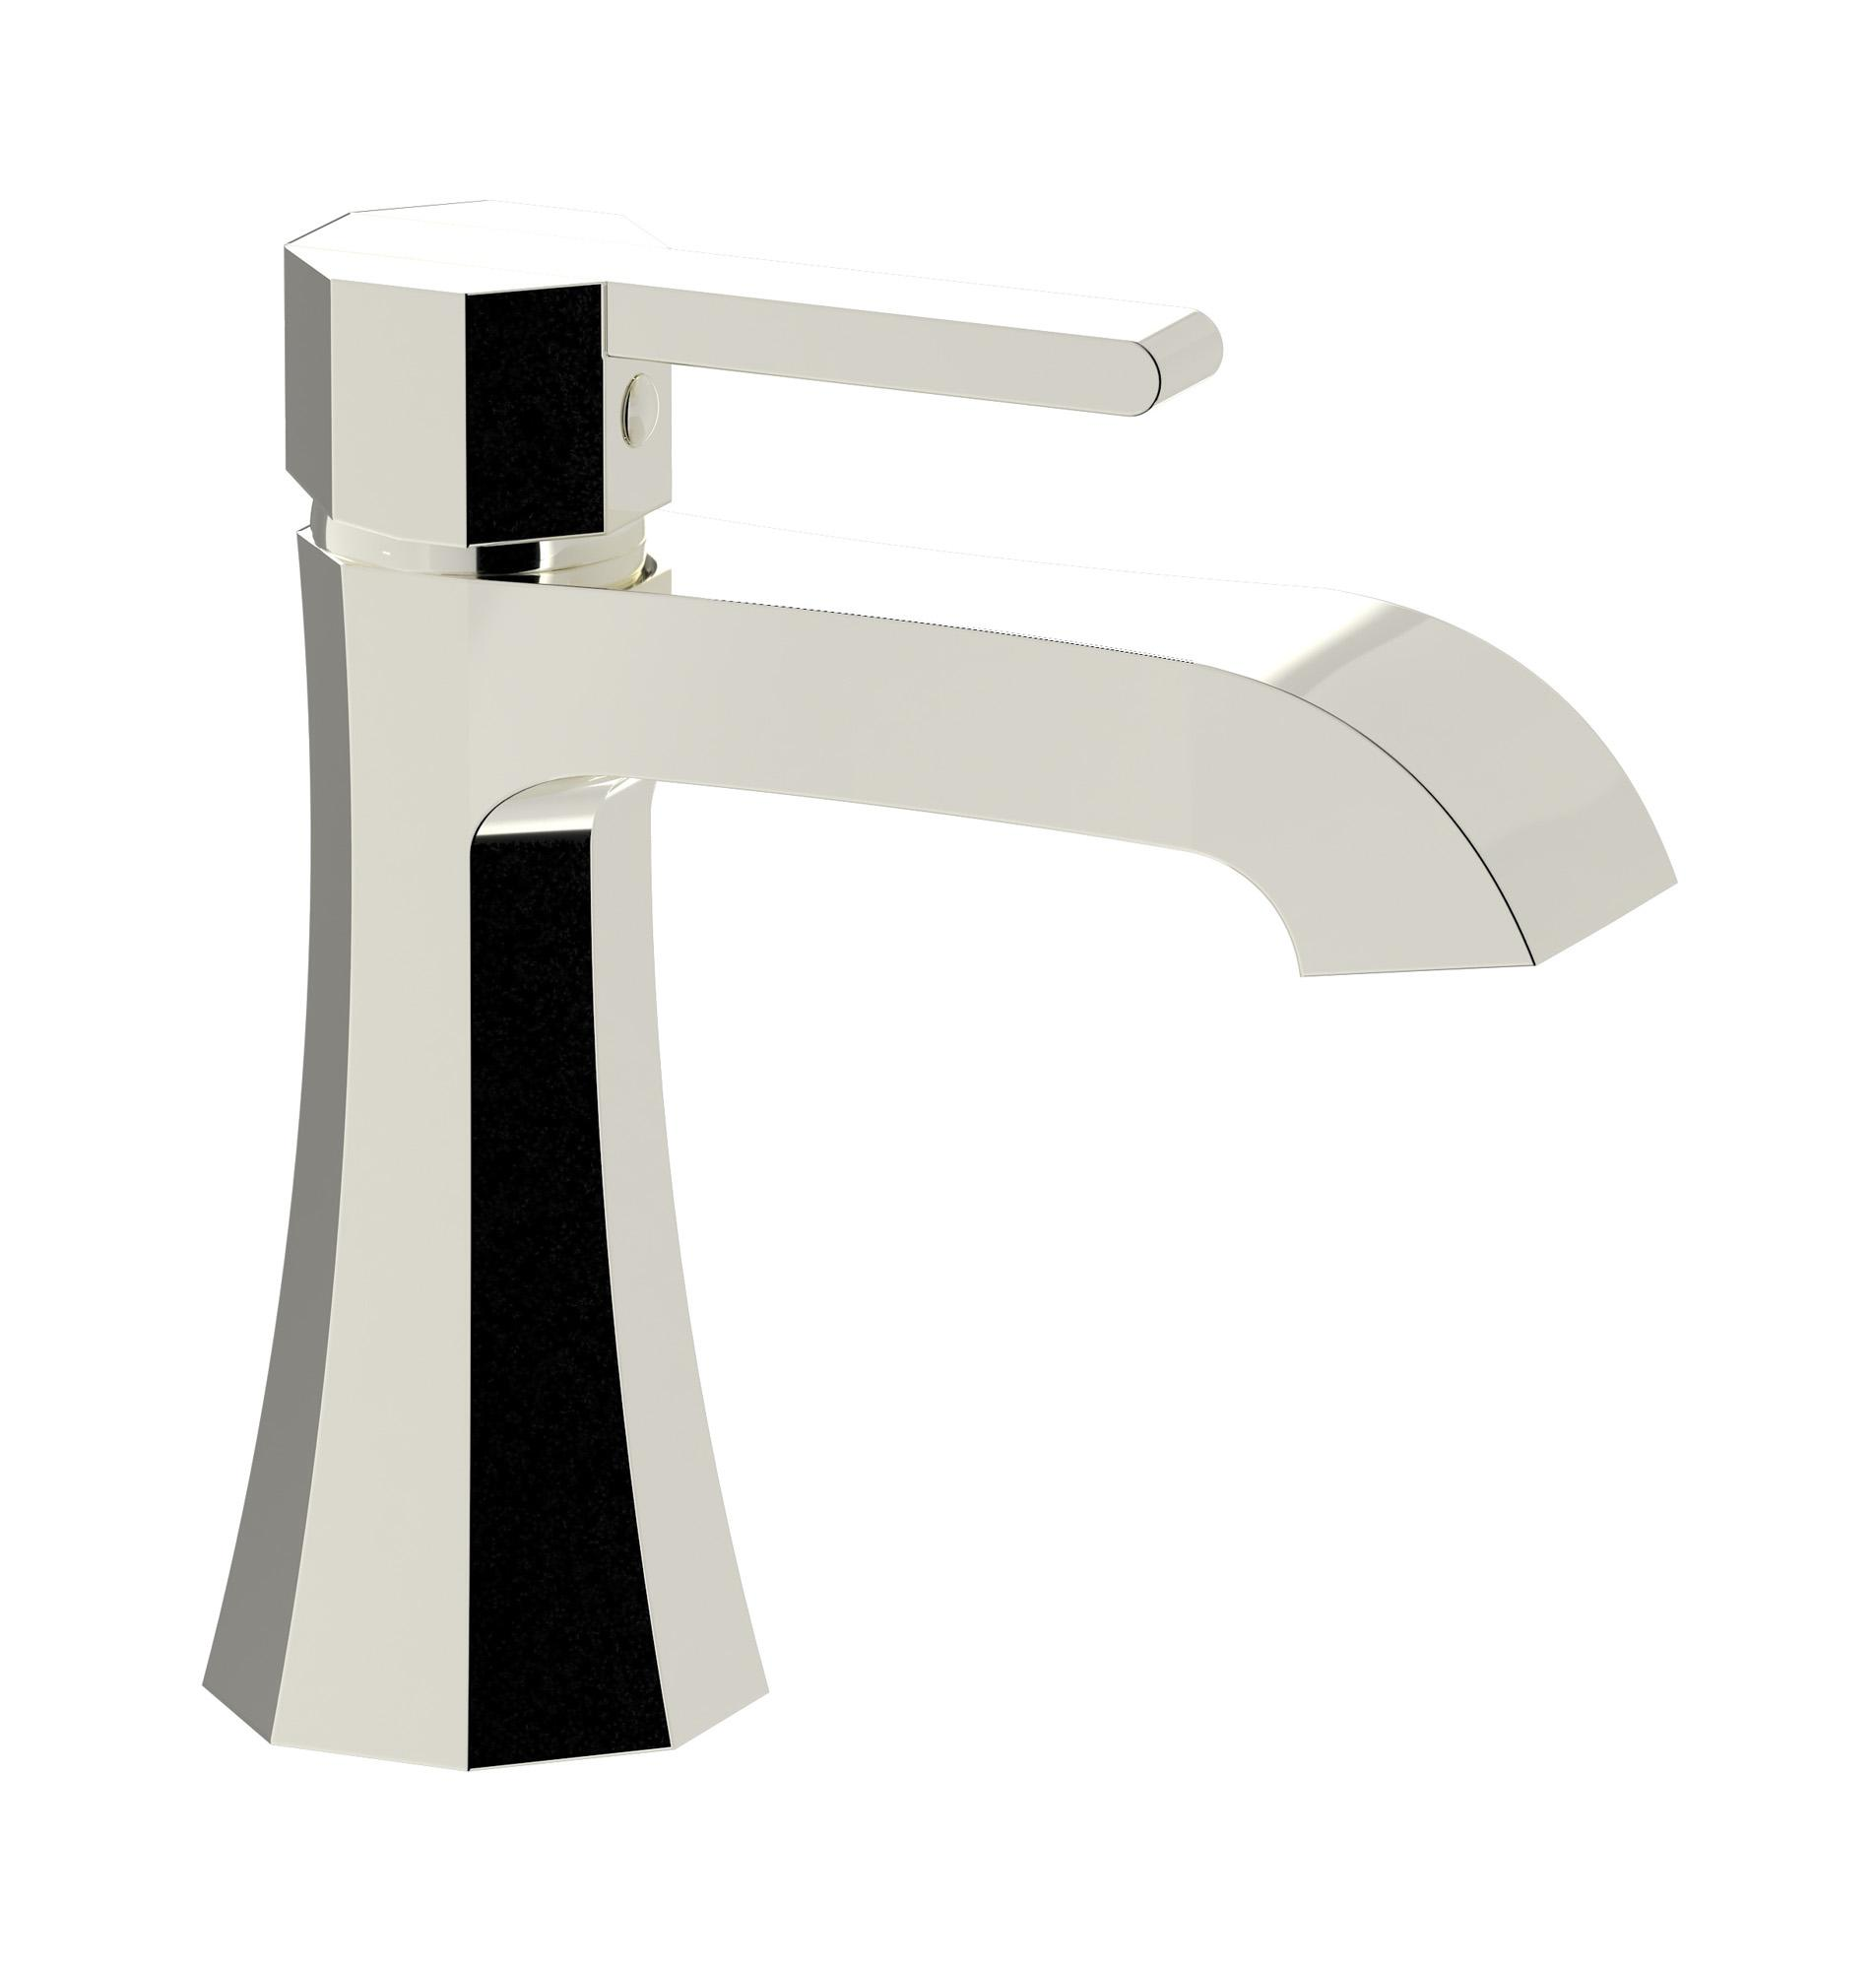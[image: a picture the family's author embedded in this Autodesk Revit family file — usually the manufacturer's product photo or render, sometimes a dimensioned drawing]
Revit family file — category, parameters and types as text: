
# Revit family: BL200
name_source: partatom
category: Apparecchi idraulici
units: mm (PartAtom-declared; Revit-internal decimal feet)

## family parameters
Basato su piano di lavoro = No
Condiviso = No
Mantieni orientamento annotazione = No
Numero OmniClass = 23.45.55.17
Punto di calcolo locali = No
Quota connettore circolare = Usa diametro
Sempre verticale = Sì
Taglio con vuoti quando caricato = No
Tipo di parte = Normale
Titolo OmniClass = Mixing Faucets

## types (7) — shared parameters
Cold water inlet = 10 mm  [stored 0.0328084 ft]
Commenti sul tipo = Washbasin
Connessione CW = No
Connessione HW = No
Connessione di scarico = No
Connessione di ventilazione = No
Descrizione = Monohole washbasin mixer complete with drain
Hot water inlet = 10 mm  [stored 0.0328084 ft]
Produttore = IB Rubinetterie S.p.A.
URL = https://www.weareib.it
zero-valued in all types: Prospetto di default

## per-type parameters (varying)
| type | Finishes surface | Immagine tipo | Modello |
| Chrome | IB_Chrome | BL200CC.jpg | BL200CC |
| Platinum | IB_Platinum | BL200PL.jpg | BL200PL |
| Pale gold | IB_Pale gold | BL200II.jpg | BL200II |
| Rose gold | IB_Rose gold | BL200RS.jpg | BL200RS |
| Gold | IB_gold | BL200OO.jpg | BL200OO |
| Modern Bronze | IB_Modern bronze | BL200MB.jpg | BL200MB |
| Brushed Nickel | IB_Brushed nickel | BL200SS.jpg | BL200SS |

note: [stored X ft] marks values corroborated as IEEE doubles in the binary element streams (Revit-internal decimal feet)
